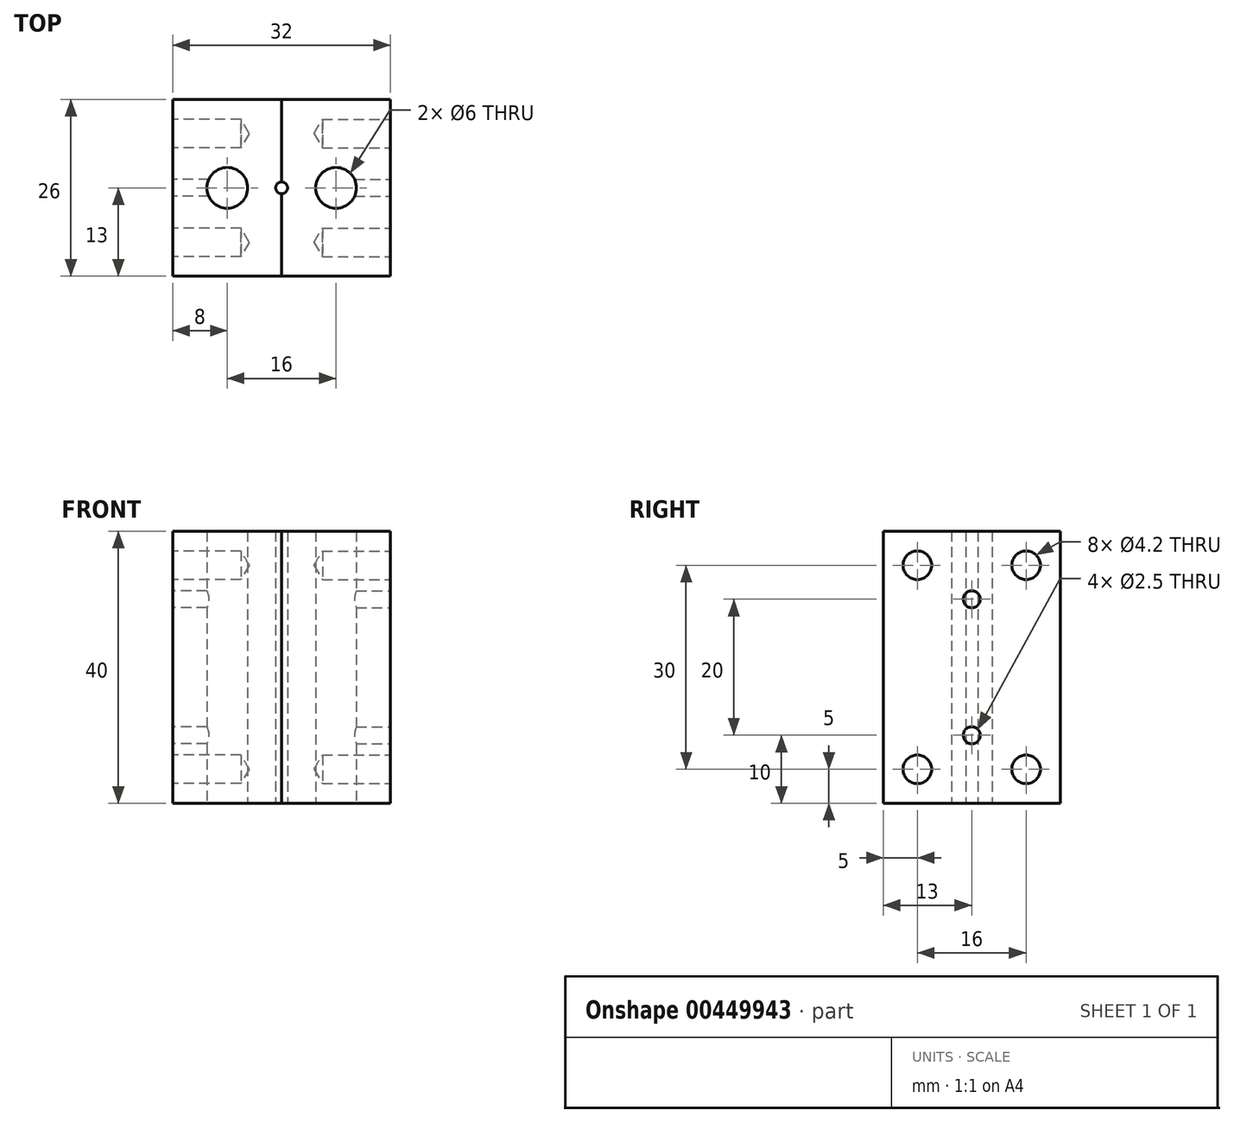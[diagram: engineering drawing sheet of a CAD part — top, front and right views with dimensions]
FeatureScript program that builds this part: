
annotation { "Feature Type Name" : "Feature", "Feature Type Description" : "" }
export const myFeature = defineFeature(function(context is Context, id is Id, definition is map)
    precondition{}
    {
        {
            var Q0;
            Q0=qCreatedBy(makeId("Top.planeOp"),FACE);
            var sketch = newSketch(context, id + "F0", { "sketchPlane" : qUnion([Q0])});
            skLineSegment(sketch, "E0.bottom", {"start": v(-16, 13) * mm, "end": v(16, 13) * mm});
            skLineSegment(sketch, "E0.top", {"start": v(-16, -13) * mm, "end": v(16, -13) * mm});
            skLineSegment(sketch, "E0.left", {"start": v(-16, 13) * mm, "end": v(-16, -13) * mm});
            skLineSegment(sketch, "E0.right", {"start": v(16, 13) * mm, "end": v(16, -13) * mm});
            skLineSegment(sketch, "E1", {"start": v(0, 13) * mm, "end": v(0, -13) * mm});
            skPoint(sketch, "E2", {"position": v(0, 0) * mm});
            skCircle(sketch, "E3", {"center": v(0, 0) * mm, "radius": 0.87 * mm});
            skCircle(sketch, "E4", {"center": v(-8, 0) * mm, "radius": 3 * mm});
            skCircle(sketch, "E5", {"center": v(8, 0) * mm, "radius": 3 * mm});
            skLineSegment(sketch, "E6", {"start": v(-8, 0) * mm, "end": v(0, 0) * mm, "construction": true});
            skLineSegment(sketch, "E7", {"start": v(0, 0) * mm, "end": v(8, 0) * mm, "construction": true});
            skSolve(sketch);
        }
        {
            var Q0;
            {var subQ5=sQuery(id+"F0.wireOp",EDGE,"E0.left");Q0=makeQuery(id+"F0.imprint","IMPRINT",FACE,{"disambiguationData":[TD([[makeQuery(id+"F0.imprint","IMPRINT",EDGE,{"derivedFrom":subQ5}),1.0]])]});}
            extrude(context, id + "F1", {"entities" : qUnion([Q0]), "depth" : 40 * mm});
        }
        {
            var Q0;
            Q0=makeQuery(id+"F1.opExtrude","SWEPT_FACE",FACE,{"disambiguationData":[OSD([sQuery(id+"F0.wireOp",EDGE,"E0.left")])]});
            var sketch = newSketch(context, id + "F2", { "sketchPlane" : qUnion([Q0])});
            skPoint(sketch, "E8", {"position": v(-8, 35) * mm});
            skPoint(sketch, "E9", {"position": v(-8, 5) * mm});
            skPoint(sketch, "E10", {"position": v(8, 35) * mm});
            skPoint(sketch, "E11", {"position": v(8, 5) * mm});
            skPoint(sketch, "E12", {"position": v(0, 30) * mm});
            skPoint(sketch, "E13", {"position": v(13, 20) * mm});
            skPoint(sketch, "E14", {"position": v(0, 10) * mm});
            skLineSegment(sketch, "E15", {"start": v(0, 30) * mm, "end": v(0, 20) * mm, "construction": true});
            skLineSegment(sketch, "E16", {"start": v(0, 20) * mm, "end": v(0, 10) * mm, "construction": true});
            skSolve(sketch);
        }
        {
            var Q0;
            Q0=sQuery(id+"F2.wireOp",VERTEX,"E8");
            var Q1;
            Q1=sQuery(id+"F2.wireOp",VERTEX,"E10");
            var Q2;
            Q2=sQuery(id+"F2.wireOp",VERTEX,"E11");
            var Q3;
            Q3=sQuery(id+"F2.wireOp",VERTEX,"E9");
            var Q4;
            Q4=makeQuery(id+"F1.opExtrude","SWEPT_BODY",BODY,{"disambiguationData":[OSD([sQuery(id+"F0.wireOp",EDGE,"E0.bottom"),sQuery(id+"F0.wireOp",EDGE,"E0.top"),sQuery(id+"F0.wireOp",EDGE,"E0.left"),sQuery(id+"F0.wireOp",EDGE,"E1"),sQuery(id+"F0.wireOp",EDGE,"E3"),sQuery(id+"F0.wireOp",EDGE,"E4")])]});
            hole(context, id + "F3", {"style" : HoleStyle.SIMPLE, "endStyle" : HoleEndStyle.BLIND, "standardTappedOrClearance" : lookupTablePath({ "standard" : "ISO", "engagement" : "75%", "pitch" : "0.8 mm", "size" : "M5", "type" : "Tapped" }), "standardBlindInLast" : lookupTablePath({ "standard" : "ISO", "engagement" : "75%", "pitch" : "0.8 mm", "size" : "M5", "type" : "Tapped" }), "holeDiameter" : 4.2 * mm, "showTappedDepth" : true, "holeDepth" : 10 * mm, "isTappedThrough" : true, "tappedDepth" : 7.6 * mm, "tapClearance" : 3, "startFromSketch" : true, "locations" : qUnion([Q0, Q1, Q2, Q3]), "scope" : qUnion([Q4]), "majorDiameter" : 5 * mm});
        }
        {
            var Q0;
            Q0=sQuery(id+"F2.wireOp",VERTEX,"E12");
            var Q1;
            Q1=sQuery(id+"F2.wireOp",VERTEX,"E14");
            var Q2;
            Q2=makeQuery(id+"F1.opExtrude","SWEPT_BODY",BODY,{"disambiguationData":[OSD([sQuery(id+"F0.wireOp",EDGE,"E0.bottom"),sQuery(id+"F0.wireOp",EDGE,"E0.top"),sQuery(id+"F0.wireOp",EDGE,"E0.left"),sQuery(id+"F0.wireOp",EDGE,"E1"),sQuery(id+"F0.wireOp",EDGE,"E3"),sQuery(id+"F0.wireOp",EDGE,"E4")])]});
            hole(context, id + "F4", {"style" : HoleStyle.SIMPLE, "endStyle" : HoleEndStyle.BLIND, "standardTappedOrClearance" : lookupTablePath({ "standard" : "ISO", "engagement" : "75%", "pitch" : "0.5 mm", "size" : "M3", "type" : "Tapped" }), "standardBlindInLast" : lookupTablePath({ "standard" : "ISO", "engagement" : "75%", "pitch" : "0.5 mm", "size" : "M3", "type" : "Tapped" }), "holeDiameter" : 2.5 * mm, "showTappedDepth" : true, "holeDepth" : 10 * mm, "isTappedThrough" : true, "tappedDepth" : 8.5 * mm, "tapClearance" : 3, "startFromSketch" : true, "locations" : qUnion([Q0, Q1]), "scope" : qUnion([Q2]), "majorDiameter" : 3 * mm});
        }
        {
            var Q0;
            Q0=makeQuery(id+"F1.opExtrude","SWEPT_BODY",BODY,{"disambiguationData":[OSD([sQuery(id+"F0.wireOp",EDGE,"E0.bottom"),sQuery(id+"F0.wireOp",EDGE,"E0.top"),sQuery(id+"F0.wireOp",EDGE,"E0.left"),sQuery(id+"F0.wireOp",EDGE,"E1"),sQuery(id+"F0.wireOp",EDGE,"E3"),sQuery(id+"F0.wireOp",EDGE,"E4")])]});
            var Q1;
            Q1=qCreatedBy(makeId("Right.planeOp"),FACE);
            mirror(context, id + "F5", {"entities" : qUnion([Q0]), "mirrorPlane" : qUnion([Q1])});
        }
    });
